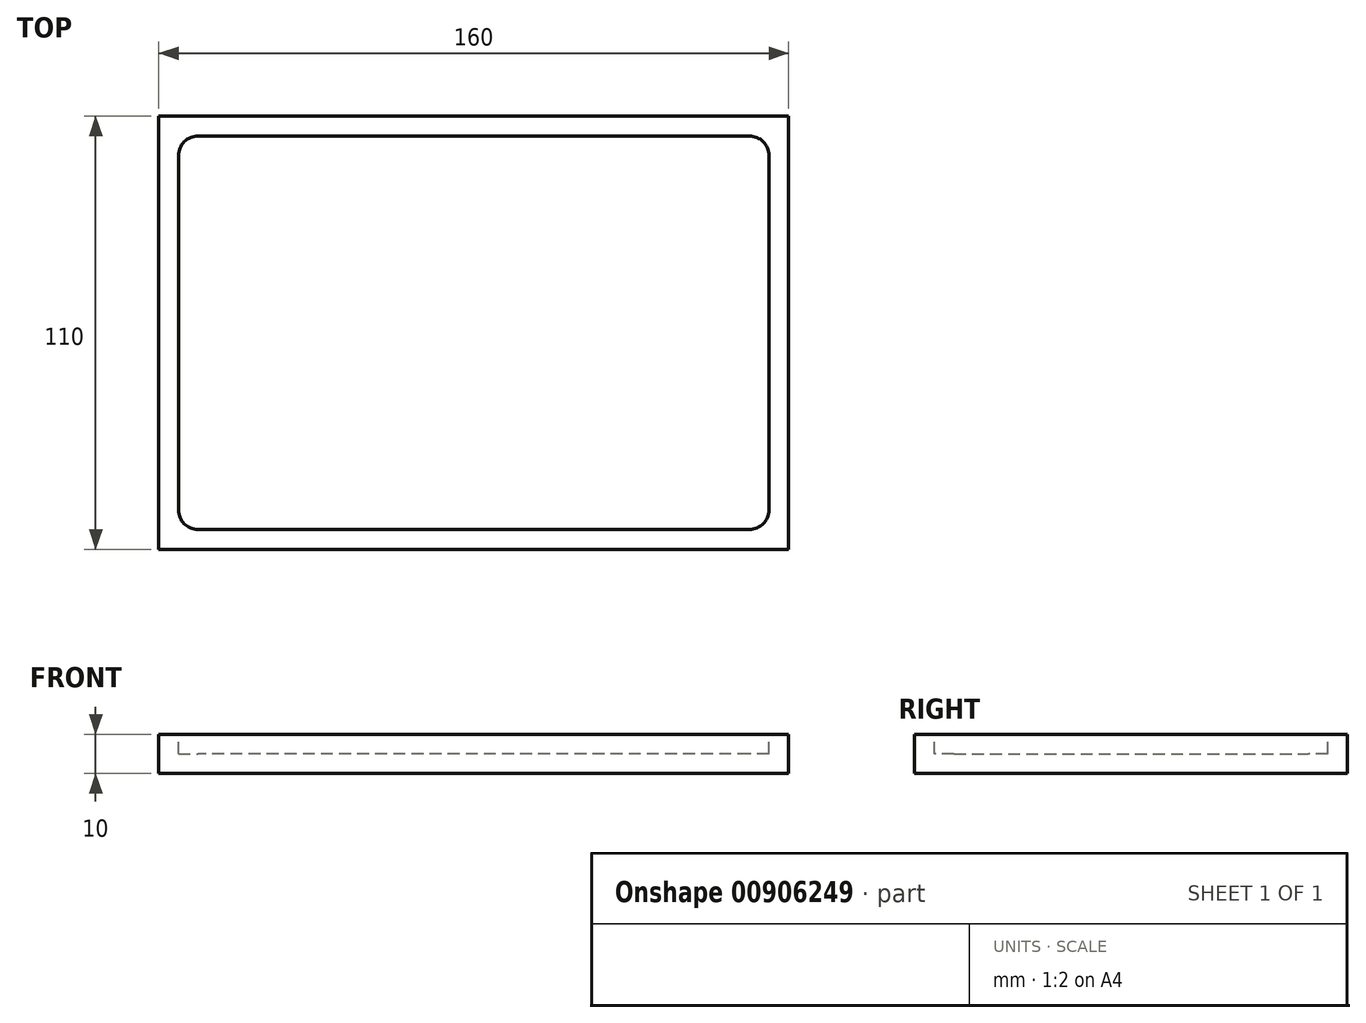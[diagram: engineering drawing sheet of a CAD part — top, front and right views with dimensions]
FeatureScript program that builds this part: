
annotation { "Feature Type Name" : "Feature", "Feature Type Description" : "" }
export const myFeature = defineFeature(function(context is Context, id is Id, definition is map)
    precondition{}
    {
        {
            var Q0;
            Q0=qCreatedBy(makeId("Top.planeOp"),FACE);
            var sketch = newSketch(context, id + "F0", { "sketchPlane" : qUnion([Q0])});
            skLineSegment(sketch, "E0.bottom", {"start": v(-70, 50) * mm, "end": v(70, 50) * mm});
            skLineSegment(sketch, "E0.top", {"start": v(-70, -50) * mm, "end": v(70, -50) * mm});
            skLineSegment(sketch, "E0.left", {"start": v(-75, 45) * mm, "end": v(-75, -45) * mm});
            skLineSegment(sketch, "E0.right", {"start": v(75, 45) * mm, "end": v(75, -45) * mm});
            skPoint(sketch, "E1.visualSharp", {"position": v(-75, 50) * mm});
            skArc(sketch, "E1.filletArc", {"start": v(-70, 50) * mm, "mid": v(-73.54, 48.54) * mm, "end": v(-75, 45) * mm});
            skPoint(sketch, "E2.visualSharp", {"position": v(-75, -50) * mm});
            skArc(sketch, "E2.filletArc", {"start": v(-75, -45) * mm, "mid": v(-73.54, -48.54) * mm, "end": v(-70, -50) * mm});
            skPoint(sketch, "E3.visualSharp", {"position": v(75, -50) * mm});
            skArc(sketch, "E3.filletArc", {"start": v(70, -50) * mm, "mid": v(73.54, -48.54) * mm, "end": v(75, -45) * mm});
            skPoint(sketch, "E4.visualSharp", {"position": v(75, 50) * mm});
            skArc(sketch, "E4.filletArc", {"start": v(75, 45) * mm, "mid": v(73.54, 48.54) * mm, "end": v(70, 50) * mm});
            skLineSegment(sketch, "E5.bottom", {"start": v(-80, -55) * mm, "end": v(80, -55) * mm});
            skLineSegment(sketch, "E5.top", {"start": v(-80, 55) * mm, "end": v(80, 55) * mm});
            skLineSegment(sketch, "E5.left", {"start": v(-80, -55) * mm, "end": v(-80, 55) * mm});
            skLineSegment(sketch, "E5.right", {"start": v(80, -55) * mm, "end": v(80, 55) * mm});
            skSolve(sketch);
        }
        {
            var Q0;
            Q0 = qSketchRegion(id + "F0", true);
            extrude(context, id + "F1", {"entities" : qUnion([Q0]), "depth" : -10 * mm, "offsetDistance" : 25 * mm});
        }
        {
            var Q0;
            Q0=makeQuery(id+"F0.imprint","IMPRINT",FACE,{"disambiguationData":[TD([[makeQuery(id+"F0.imprint","IMPRINT",EDGE,{"derivedFrom":sQuery(id+"F0.wireOp",EDGE,"E0.bottom")}),1.0]])]});
            var Q1;
            Q1=makeQuery(id+"F0.imprint","IMPRINT",FACE,{"disambiguationData":[TD([[makeQuery(id+"F0.imprint","IMPRINT",EDGE,{"derivedFrom":sQuery(id+"F0.wireOp",EDGE,"E0.bottom")}),-1.0]])]});
            extrude(context, id + "F2", {"entities" : qUnion([Q0, Q1]), "operationType" : NewBodyOperationType.ADD, "oppositeDirection" : true, "depth" : 10 * mm, "offsetDistance" : 25 * mm, "hasSecondDirection" : true, "secondDirectionOppositeDirection" : true, "secondDirectionDepth" : 5 * mm});
        }
    });
